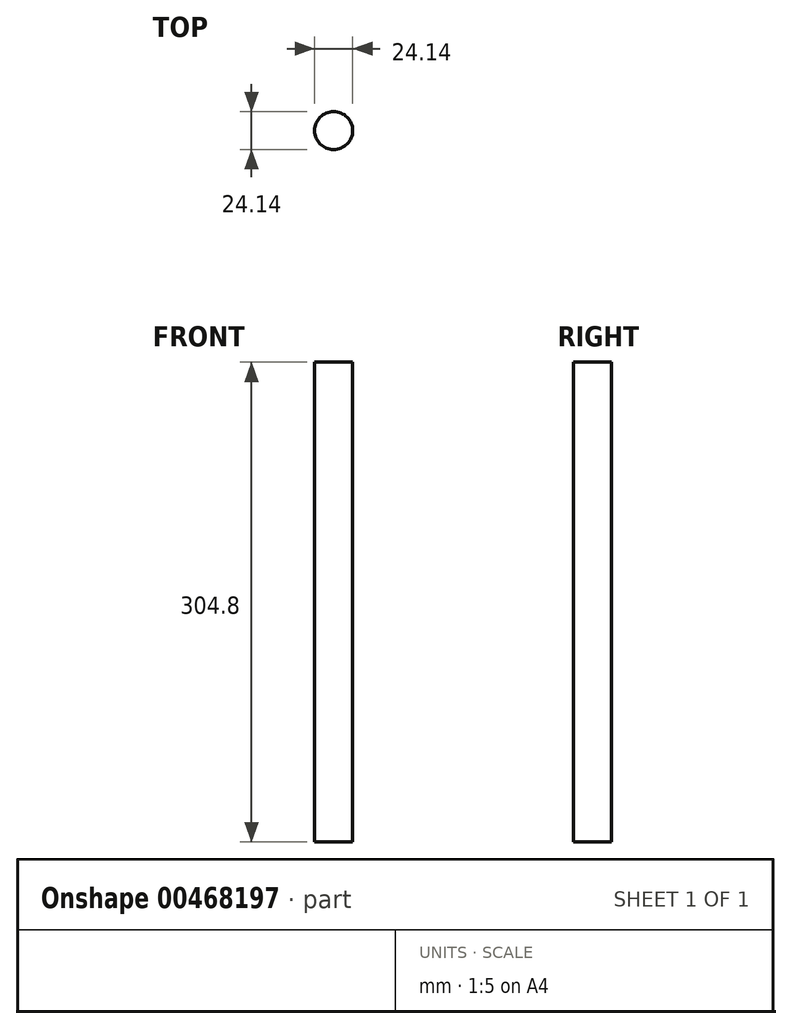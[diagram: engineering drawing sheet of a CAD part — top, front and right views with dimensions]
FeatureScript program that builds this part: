
annotation { "Feature Type Name" : "Feature", "Feature Type Description" : "" }
export const myFeature = defineFeature(function(context is Context, id is Id, definition is map)
    precondition{}
    {
        {
            var Q0;
            Q0=qCreatedBy(makeId("Top.planeOp"),FACE);
            var sketch = newSketch(context, id + "F0", { "sketchPlane" : qUnion([Q0])});
            skCircle(sketch, "E0", {"center": v(0, 0) * mm, "radius": 12.07 * mm});
            skSolve(sketch);
        }
        {
            var Q0;
            Q0=makeQuery(id+"F0.imprint","IMPRINT",FACE,{"disambiguationData":[TD([[makeQuery(id+"F0.imprint","IMPRINT",EDGE,{"derivedFrom":sQuery(id+"F0.wireOp",EDGE,"E0")}),1.0]])]});
            extrude(context, id + "F1", {"entities" : qUnion([Q0]), "depth" : 304.8 * mm});
        }
    });
